# Revit family: 32-60-010-DN80-450
name_source: partatom
category: Pipe Accessories
units: mm (PartAtom-declared; Revit-internal decimal feet)

## family parameters
Always vertical = No
Cut with Voids When Loaded = No
Part Type = Valve - Breaks Into
Round Connector Dimension = Use Diameter
Shared = No
Work Plane-Based = No

## types (9) — shared parameters
32-080-60-0141099 = DN080_PN16
32-100-60-0141099 = DN100_PN16
32-150-60-0141099 = DN150_PN16
32-200-60-0141099 = DN200_PN16
32-225-60-0141099 = DN225_PN16
32-250-60-01610 = DN250_PN16
32-300-60-01610 = DN300_PN16
32-400-60-01610 = DN400_PN16
32-450-60-01610 = DN450_PN16
Body_Wallthickness = 15 mm  [stored 0.0492126 ft]
Description_ = AVK GATE VALVE, SHORT SPIGOT ENDS
E = 15 mm  [stored 0.0492126 ft]
Ftc = 4 mm  [stored 0.0131234 ft]
Name_Height_reference = 10 mm  [stored 0.0328084 ft]
Rib_Thickness = 18 mm  [stored 0.0590551 ft]
Search_table = 32-60-010-DN80-450
URL product pages = https://www.avkvalves.com
zero-valued in all types: Bottom_Reference

## per-type parameters (varying)
- DN080_PN16: At=70 mm; Body_Height=132 mm; Body_depth=140 mm; Body_width=75 mm; Body_width_ref=90 mm; Bonnet_Flange_Depth=171 mm; Bonnet_Flange_Width=90 mm; Bonnet_Flange_cut=8 mm  [stored 0.0262467 ft]; Bonnet_Flange_thickness=15 mm  [stored 0.0492126 ft]; Bonnet_Height=50 mm; Bonnet_Reference_height=122 mm; Bonnet_Thickness=77 mm; Bt=77 mm; Bt_2=69 mm; CL _Thickness=27 mm  [stored 0.0885827 ft]; CL_Height=75 mm; Cut_Reference=560 mm; D=53 mm; D2=34 mm  [stored 0.111549 ft]; D_ref=50 mm; D_ref_2=50 mm; F=9 mm; F1=10 mm  [stored 0.0328084 ft]; F1_ref=20 mm  [stored 0.0656168 ft]; Fillet_Thickness=6 mm  [stored 0.019685 ft]; Flange_OR=100 mm; Flange_Thickness=19 mm  [stored 0.062336 ft]; Flange_Thickness_cut=30 mm  [stored 0.0984252 ft]; Ftc_reference_height=100 mm; H=282 mm; H1=248 mm; H3=338 mm; H3_ref=56 mm; Horizontal_Flange_width=112 mm; ID=40 mm  [stored 0.131234 ft]; L=280 mm; L1=91 mm; L2=140 mm; L_Dia=80 mm; L_ref=140 mm; Name_Reference=90 mm; Name_Width=38 mm  [stored 0.124672 ft]; Neck_H=41 mm; Neck_T=25 mm  [stored 0.082021 ft]; Neck_T2=23 mm  [stored 0.0754593 ft]; Nominal Diameter (DN)=80 mm; R1tv=1000 mm; R2f=15 mm  [stored 0.0492126 ft]; RF_Dia=66 mm; Rf=187 mm; Rib_Height_Reference_1=120 mm; Rib_Height_Reference_2=110 mm; Rib_Height_Reference_3=100 mm; Rib_Height_Reference_4=85 mm; Rib_Width_1=38 mm  [stored 0.124672 ft]; Rib_Width_2=38 mm  [stored 0.124672 ft]; Rib_Width_3=38 mm  [stored 0.124672 ft]; Rib_depth_1=38 mm  [stored 0.124672 ft]; Rib_depth_2=38 mm  [stored 0.124672 ft]; Rib_depth_3=38 mm  [stored 0.124672 ft]; Rt=333 mm; S=3 mm  [stored 0.00984252 ft]
- DN100_PN16: At=83 mm; Body_Height=148 mm; Body_depth=166 mm; Body_width=80 mm; Body_width_ref=96 mm; Bonnet_Flange_Depth=192 mm; Bonnet_Flange_Width=100 mm; Bonnet_Flange_cut=8 mm  [stored 0.0262467 ft]; Bonnet_Flange_thickness=15 mm  [stored 0.0492126 ft]; Bonnet_Height=55 mm; Bonnet_Reference_height=138 mm; Bonnet_Thickness=82 mm; Bt=82 mm; Bt_2=74 mm; CL _Thickness=29 mm  [stored 0.0951444 ft]; CL_Height=88 mm; Cut_Reference=600 mm; D=63 mm; D2=38 mm  [stored 0.124672 ft]; D_ref=60 mm; D_ref_2=60 mm; F=10 mm  [stored 0.0328084 ft]; F1=11 mm  [stored 0.0360892 ft]; F1_ref=22 mm  [stored 0.0721785 ft]; Fillet_Thickness=6 mm  [stored 0.019685 ft]; Flange_OR=110 mm; Flange_Thickness=19 mm  [stored 0.062336 ft]; Flange_Thickness_cut=30 mm  [stored 0.0984252 ft]; Ftc_reference_height=110 mm; H=305 mm; H1=267 mm; H3=370 mm; H3_ref=65 mm; Horizontal_Flange_width=130 mm; ID=50 mm; L=300 mm; L1=93 mm; L2=150 mm; L_Dia=100 mm; L_ref=150 mm; Name_Reference=101 mm; Name_Width=40 mm  [stored 0.131234 ft]; Neck_H=31 mm  [stored 0.101706 ft]; Neck_T=27 mm  [stored 0.0885827 ft]; Neck_T2=25 mm  [stored 0.082021 ft]; Nominal Diameter (DN)=100 mm; R1tv=1100 mm; R2f=15 mm  [stored 0.0492126 ft]; RF_Dia=78 mm; Rf=217 mm; Rib_Height_Reference_1=120 mm; Rib_Height_Reference_2=110 mm; Rib_Height_Reference_3=100 mm; Rib_Height_Reference_4=90 mm; Rib_Width_1=40 mm  [stored 0.131234 ft]; Rib_Width_2=40 mm  [stored 0.131234 ft]; Rib_Width_3=40 mm  [stored 0.131234 ft]; Rib_depth_1=40 mm  [stored 0.131234 ft]; Rib_depth_2=40 mm  [stored 0.131234 ft]; Rib_depth_3=40 mm  [stored 0.131234 ft]; Rt=367 mm; S=4 mm  [stored 0.0131234 ft]
- DN150_PN16: At=121 mm; Body_Height=200 mm; Body_depth=242 mm; Body_width=95 mm; Body_width_ref=114 mm; Bonnet_Flange_Depth=272 mm; Bonnet_Flange_Width=130 mm; Bonnet_Flange_cut=8 mm  [stored 0.0262467 ft]; Bonnet_Flange_thickness=15 mm  [stored 0.0492126 ft]; Bonnet_Height=71 mm; Bonnet_Reference_height=190 mm; Bonnet_Thickness=97 mm; Bt=97 mm; Bt_2=89 mm; CL _Thickness=34 mm  [stored 0.111549 ft]; CL_Height=126 mm; Cut_Reference=700 mm; D=89 mm; D2=38 mm  [stored 0.124672 ft]; D_ref=85 mm; D_ref_2=86 mm; F=10 mm  [stored 0.0328084 ft]; F1=11 mm  [stored 0.0360892 ft]; F1_ref=22 mm  [stored 0.0721785 ft]; Fillet_Thickness=12 mm  [stored 0.0393701 ft]; Flange_OR=142 mm; Flange_Thickness=19 mm  [stored 0.062336 ft]; Flange_Thickness_cut=34 mm  [stored 0.111549 ft]; Ftc_reference_height=142 mm; H=400 mm; H1=362 mm; H3=491 mm; H3_ref=91 mm; Horizontal_Flange_width=182 mm; ID=75 mm; L=350 mm; L1=101 mm; L2=175 mm; L_Dia=150 mm; L_ref=175 mm; Name_Reference=143 mm; Name_Width=48 mm; Neck_H=36 mm; Neck_T=32 mm  [stored 0.104987 ft]; Neck_T2=30 mm  [stored 0.0984252 ft]; Nominal Diameter (DN)=150 mm; R1tv=1420 mm; R2f=30 mm  [stored 0.0984252 ft]; RF_Dia=106 mm; Rf=303 mm; Rib_Height_Reference_1=120 mm; Rib_Height_Reference_2=110 mm; Rib_Height_Reference_3=100 mm; Rib_Height_Reference_4=150 mm; Rib_Width_1=48 mm; Rib_Width_2=48 mm; Rib_Width_3=48 mm; Rib_depth_1=48 mm; Rib_depth_2=48 mm; Rib_depth_3=48 mm; Rt=473 mm; S=5 mm  [stored 0.0164042 ft]
- DN200_PN16: At=147 mm; Body_Height=260 mm; Body_depth=294 mm; Body_width=108 mm; Body_width_ref=130 mm; Bonnet_Flange_Depth=332 mm; Bonnet_Flange_Width=140 mm; Bonnet_Flange_cut=13 mm; Bonnet_Flange_thickness=25 mm  [stored 0.082021 ft]; Bonnet_Height=85 mm; Bonnet_Reference_height=250 mm; Bonnet_Thickness=110 mm; Bt=110 mm; Bt_2=102 mm; CL _Thickness=34 mm  [stored 0.111549 ft]; CL_Height=152 mm; Cut_Reference=800 mm; D=117 mm; D2=42 mm  [stored 0.137795 ft]; D_ref=110 mm; D_ref_2=114 mm; F=12 mm  [stored 0.0393701 ft]; F1=14 mm  [stored 0.0459318 ft]; F1_ref=28 mm  [stored 0.0918635 ft]; Fillet_Thickness=24 mm  [stored 0.0787402 ft]; Flange_OR=170 mm; Flange_Thickness=20 mm  [stored 0.0656168 ft]; Flange_Thickness_cut=35 mm  [stored 0.114829 ft]; Ftc_reference_height=170 mm; H=490 mm; H1=448 mm; H3=608 mm; H3_ref=118 mm; Horizontal_Flange_width=236 mm; ID=100 mm; L=400 mm; L1=111 mm; L2=200 mm; L_Dia=200 mm; L_ref=200 mm; Name_Reference=183 mm; Name_Width=54 mm; Neck_H=36 mm; Neck_T=32 mm  [stored 0.104987 ft]; Neck_T2=30 mm  [stored 0.0984252 ft]; Nominal Diameter (DN)=200 mm; R1tv=1700 mm; R2f=60 mm; RF_Dia=133 mm; Rf=393 mm; Rib_Height_Reference_1=120 mm; Rib_Height_Reference_2=110 mm; Rib_Height_Reference_3=100 mm; Rib_Height_Reference_4=180 mm; Rib_Width_1=54 mm; Rib_Width_2=54 mm; Rib_Width_3=54 mm; Rib_depth_1=54 mm; Rib_depth_2=54 mm; Rib_depth_3=54 mm; Rt=567 mm; S=6 mm  [stored 0.019685 ft]
- DN225_PN16: At=175 mm; Body_Height=290 mm; Body_depth=350 mm; Body_width=115 mm; Body_width_ref=138 mm; Bonnet_Flange_Depth=470 mm; Bonnet_Flange_Width=155 mm; Bonnet_Flange_cut=13 mm; Bonnet_Flange_thickness=25 mm  [stored 0.082021 ft]; Bonnet_Height=93 mm; Bonnet_Reference_height=280 mm; Bonnet_Thickness=117 mm; Bt=117 mm; Bt_2=109 mm; CL _Thickness=38 mm  [stored 0.124672 ft]; CL_Height=180 mm; Cut_Reference=850 mm; D=128 mm; D2=47 mm; D_ref=123 mm; D_ref_2=125 mm; F=14 mm  [stored 0.0459318 ft]; F1=16 mm  [stored 0.0524934 ft]; F1_ref=31 mm  [stored 0.101706 ft]; Fillet_Thickness=24 mm  [stored 0.0787402 ft]; Flange_OR=185 mm; Flange_Thickness=22 mm  [stored 0.0721785 ft]; Flange_Thickness_cut=36 mm; Ftc_reference_height=185 mm; H=616 mm; H1=569 mm; H3=785 mm; H3_ref=169 mm; Horizontal_Flange_width=338 mm; ID=113 mm; L=425 mm; L1=98 mm; L2=200 mm; L_Dia=225 mm; L_ref=213 mm; Name_Reference=192 mm; Name_Width=58 mm; Neck_H=99 mm; Neck_T=36 mm; Neck_T2=34 mm  [stored 0.111549 ft]; Nominal Diameter (DN)=225 mm; R1tv=1850 mm; R2f=60 mm; RF_Dia=145 mm; Rf=563 mm; Rib_Height_Reference_1=120 mm; Rib_Height_Reference_2=110 mm; Rib_Height_Reference_3=100 mm; Rib_Height_Reference_4=180 mm; Rib_Width_1=58 mm; Rib_Width_2=58 mm; Rib_Width_3=58 mm; Rib_depth_1=58 mm; Rib_depth_2=58 mm; Rib_depth_3=58 mm; Rt=617 mm; S=6 mm  [stored 0.019685 ft]
- DN250_PN16: At=196 mm; Body_Height=320 mm; Body_depth=392 mm; Body_width=132 mm; Body_width_ref=158 mm; Bonnet_Flange_Depth=422 mm; Bonnet_Flange_Width=175 mm; Bonnet_Flange_cut=13 mm; Bonnet_Flange_thickness=25 mm  [stored 0.082021 ft]; Bonnet_Height=100 mm; Bonnet_Reference_height=310 mm; Bonnet_Thickness=135 mm; Bt=135 mm; Bt_2=126 mm; CL _Thickness=46 mm  [stored 0.150919 ft]; CL_Height=201 mm; Cut_Reference=900 mm; D=144 mm; D2=47 mm; D_ref=135 mm; D_ref_2=141 mm; F=14 mm  [stored 0.0459318 ft]; F1=16 mm  [stored 0.0524934 ft]; F1_ref=31 mm  [stored 0.101706 ft]; Fillet_Thickness=24 mm  [stored 0.0787402 ft]; Flange_OR=200 mm; Flange_Thickness=22 mm  [stored 0.0721785 ft]; Flange_Thickness_cut=38 mm  [stored 0.124672 ft]; Ftc_reference_height=200 mm; H=664 mm; H1=617 mm; H3=810 mm; H3_ref=146 mm; Horizontal_Flange_width=292 mm; ID=125 mm; L=450 mm; L1=140 mm; L2=200 mm; L_Dia=250 mm; L_ref=225 mm; Name_Reference=200 mm; Name_Width=66 mm; Neck_H=96 mm; Neck_T=44 mm  [stored 0.144357 ft]; Neck_T2=42 mm  [stored 0.137795 ft]; Nominal Diameter (DN)=250 mm; R1tv=2000 mm; R2f=60 mm; RF_Dia=160 mm; Rf=487 mm; Rib_Height_Reference_1=90 mm; Rib_Height_Reference_2=110 mm; Rib_Height_Reference_3=100 mm; Rib_Height_Reference_4=250 mm; Rib_Width_1=150 mm; Rib_Width_2=150 mm; Rib_Width_3=66 mm; Rib_depth_1=422 mm; Rib_depth_2=66 mm; Rib_depth_3=66 mm; Rt=667 mm; S=6 mm  [stored 0.019685 ft]
- DN300_PN16: At=209 mm; Body_Height=370 mm; Body_depth=418 mm; Body_width=160 mm; Body_width_ref=192 mm; Bonnet_Flange_Depth=448 mm; Bonnet_Flange_Width=200 mm; Bonnet_Flange_cut=18 mm  [stored 0.0590551 ft]; Bonnet_Flange_thickness=35 mm  [stored 0.114829 ft]; Bonnet_Height=114 mm; Bonnet_Reference_height=360 mm; Bonnet_Thickness=163 mm; Bt=163 mm; Bt_2=154 mm; CL _Thickness=60 mm; CL_Height=214 mm; Cut_Reference=1000 mm; D=172 mm; D2=47 mm; D_ref=160 mm; D_ref_2=169 mm; F=14 mm  [stored 0.0459318 ft]; F1=16 mm  [stored 0.0524934 ft]; F1_ref=31 mm  [stored 0.101706 ft]; Fillet_Thickness=24 mm  [stored 0.0787402 ft]; Flange_OR=228 mm; Flange_Thickness=25 mm  [stored 0.082021 ft]; Flange_Thickness_cut=39 mm  [stored 0.127953 ft]; Ftc_reference_height=228 mm; H=740 mm; H1=693 mm; H3=914 mm; H3_ref=174 mm; Horizontal_Flange_width=348 mm; ID=150 mm; L=500 mm; L1=148 mm; L2=200 mm; L_Dia=300 mm; L_ref=250 mm; Name_Reference=300 mm; Name_Width=80 mm; Neck_H=109 mm; Neck_T=58 mm; Neck_T2=56 mm; Nominal Diameter (DN)=300 mm; R1tv=2275 mm; R2f=60 mm; RF_Dia=185 mm; Rf=580 mm; Rib_Height_Reference_1=113 mm; Rib_Height_Reference_2=285 mm; Rib_Height_Reference_3=100 mm; Rib_Height_Reference_4=325 mm; Rib_Width_1=210 mm; Rib_Width_2=210 mm; Rib_Width_3=80 mm; Rib_depth_1=455 mm; Rib_depth_2=455 mm; Rib_depth_3=80 mm; Rt=758 mm; S=7 mm
- DN400_PN16: At=277 mm; Body_Height=535 mm; Body_depth=554 mm; Body_width=172 mm; Body_width_ref=206 mm; Bonnet_Flange_Depth=580 mm; Bonnet_Flange_Width=198 mm; Bonnet_Flange_cut=35 mm  [stored 0.114829 ft]; Bonnet_Flange_thickness=70 mm; Bonnet_Height=145 mm; Bonnet_Reference_height=525 mm; Bonnet_Thickness=175 mm; Bt=175 mm; Bt_2=166 mm; CL _Thickness=62 mm; CL_Height=282 mm; Cut_Reference=1200 mm; D=228 mm; D2=55 mm; D_ref=210 mm; D_ref_2=225 mm; F=16 mm  [stored 0.0524934 ft]; F1=19 mm  [stored 0.062336 ft]; F1_ref=37 mm  [stored 0.121391 ft]; Fillet_Thickness=32 mm  [stored 0.104987 ft]; Flange_OR=290 mm; Flange_Thickness=28 mm  [stored 0.0918635 ft]; Flange_Thickness_cut=45 mm  [stored 0.147638 ft]; Ftc_reference_height=290 mm; H=959 mm; H1=904 mm; H3=1194 mm; H3_ref=235 mm; Horizontal_Flange_width=470 mm; ID=200 mm; L=600 mm; L1=145 mm; L2=200 mm; L_Dia=400 mm; L_ref=300 mm; Name_Reference=475 mm; Name_Width=86 mm; Neck_H=87 mm; Neck_T=60 mm; Neck_T2=58 mm; Nominal Diameter (DN)=400 mm; R1tv=2900 mm; R2f=80 mm; RF_Dia=240 mm; Rf=783 mm; Rib_Height_Reference_1=91 mm; Rib_Height_Reference_2=230 mm; Rib_Height_Reference_3=380 mm; Rib_Height_Reference_4=492 mm; Rib_Width_1=200 mm; Rib_Width_2=200 mm; Rib_Width_3=200 mm; Rib_depth_1=600 mm; Rib_depth_2=600 mm; Rib_depth_3=600 mm; Rt=967 mm; S=7 mm
- DN450_PN16: At=289 mm; Body_Height=559 mm; Body_depth=578 mm; Body_width=187 mm; Body_width_ref=224 mm; Bonnet_Flange_Depth=610 mm; Bonnet_Flange_Width=219 mm; Bonnet_Flange_cut=35 mm  [stored 0.114829 ft]; Bonnet_Flange_thickness=70 mm; Bonnet_Height=160 mm; Bonnet_Reference_height=549 mm; Bonnet_Thickness=191 mm; Bt=191 mm; Bt_2=181 mm; CL _Thickness=70 mm; CL_Height=294 mm; Cut_Reference=1300 mm; D=254 mm; D2=80 mm; D_ref=235 mm; D_ref_2=251 mm; F=20 mm  [stored 0.0656168 ft]; F1=20 mm  [stored 0.0656168 ft]; F1_ref=40 mm  [stored 0.131234 ft]; Fillet_Thickness=32 mm  [stored 0.104987 ft]; Flange_OR=320 mm; Flange_Thickness=30 mm  [stored 0.0984252 ft]; Flange_Thickness_cut=48 mm; Ftc_reference_height=320 mm; H=1096 mm; H1=1016 mm; H3=1370 mm; H3_ref=274 mm; Horizontal_Flange_width=548 mm; ID=225 mm; L=650 mm; L1=154 mm; L2=200 mm; L_Dia=450 mm; L_ref=325 mm; Name_Reference=665 mm; Name_Width=94 mm; Neck_H=163 mm; Neck_T=68 mm; Neck_T2=66 mm; Nominal Diameter (DN)=450 mm; R1tv=3200 mm; R2f=80 mm; RF_Dia=274 mm; Rf=913 mm; Rib_Height_Reference_1=172 mm; Rib_Height_Reference_2=310 mm; Rib_Height_Reference_3=475 mm; Rib_Height_Reference_4=595 mm; Rib_Width_1=186 mm; Rib_Width_2=186 mm; Rib_Width_3=186 mm; Rib_depth_1=814 mm; Rib_depth_2=814 mm; Rib_depth_3=814 mm; Rt=1067 mm; S=7 mm

note: [stored X ft] marks values corroborated as IEEE doubles in the binary element streams (Revit-internal decimal feet)

## geometry (parser evidence)
native form markers: Extrusion x1, Sweep x3
no freeform markers — native parametric forms only
